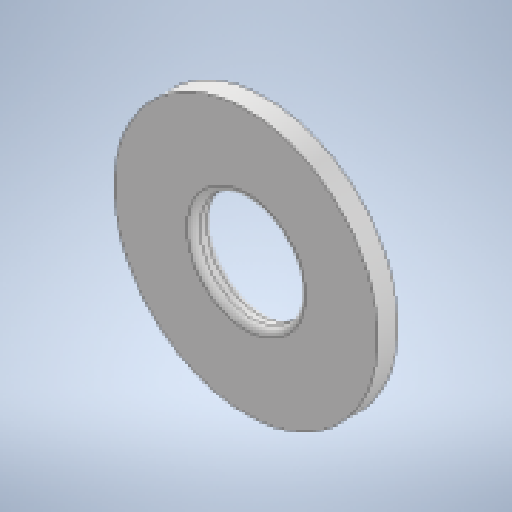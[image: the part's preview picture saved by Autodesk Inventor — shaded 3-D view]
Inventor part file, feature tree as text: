
AUTODESK INVENTOR PART (.ipt)
format: ipt  version: 2025.1 (Build 291241000, 241)  size: 145,408 bytes
history: native  units: mm
features: other x5, sketch x1, extrude x1, fillet x1, reference x1
ambient origin geometry x8: Origin, YZ Plane, XZ Plane, XY Plane, X Axis, Y Axis, Z Axis, Center Point
bodies: Body1 (feature_tree)
feature tree (9):
  other  "ソリッド1"
  sketch  "スケッチ1"
  other  "作業平面1"
  extrude  "押し出し1"  Depth=40.0mm
  fillet  "フィレット1"  Radius=10.0mm
  reference  "参照1"
  other  "<userpath>\Documents\Inventor\Vixen\doutai.iam"
  other  "doutai.iam"
  other  "02157_SmallDiameterHornB:2"
